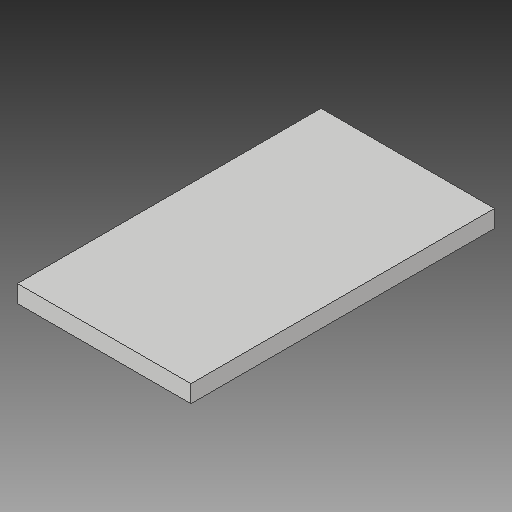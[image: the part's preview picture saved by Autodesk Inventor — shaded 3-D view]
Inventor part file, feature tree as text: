
AUTODESK INVENTOR PART (.ipt)
format: ipt  version: 2019 (Build 230136000, 136)  size: 92,160 bytes
history: native  units: mm
features: extrude x2, sketch x2
ambient origin geometry x8: Origin, YZ Plane, XZ Plane, XY Plane, X Axis, Y Axis, Z Axis, Center Point
bodies: Solid1 (feature_tree)
feature tree (4):
  extrude  "Extrusion1"  Depth=175.0mm
  extrude  "Extrusion2"  Depth=10.0mm TaperAngle=0.0deg
  sketch  "Sketch1"  dims[d0=100.0mm d1=175.0mm]
  sketch  "Sketch2"  dims[d2=7.6mm d3=10.0mm d4=0.0mm d5=10.0mm d6=0.0mm]
